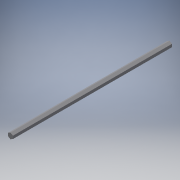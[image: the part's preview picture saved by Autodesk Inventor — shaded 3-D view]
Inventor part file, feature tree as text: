
AUTODESK INVENTOR PART (.ipt)
format: ipt  version: 2016 (Build 200138000, 138)  size: 93,696 bytes
history: native  units: in
note: dims shown in document units (in); Inventor stores cm internally (conversion verified against a paired STEP export)
features: extrude x1, sketch x1
ambient origin geometry x8: Origin, YZ Plane, XZ Plane, XY Plane, X Axis, Y Axis, Z Axis, Center Point
bodies: Solid1 (feature_tree)
feature tree (2):
  extrude  "Extrusion1"  Depth=17.0in TaperAngle=0.0deg
  sketch  "Sketch1"  dims[d0=0.5in d1=17.0in d2=0.0in]
